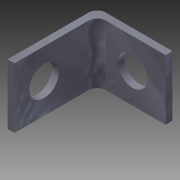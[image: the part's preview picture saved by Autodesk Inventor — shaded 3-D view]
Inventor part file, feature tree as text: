
AUTODESK INVENTOR PART (.ipt)
format: ipt  version: 2016 (Build 200138000, 138)  size: 131,072 bytes
history: native  units: mm
features: sketch x4, projected_geometry x3, extrude x2, hole x2, fillet x1
ambient origin geometry x8: Origin, YZ Plane, XZ Plane, XY Plane, X Axis, Y Axis, Z Axis, Center Point
bodies: Solid1 (feature_tree)
feature tree (12):
  extrude  "BraketBase"  Depth=10.61mm
  extrude  "BraketCut"  Depth=5.305mm
  hole  "ShortHole"  [1 undecoded]
  hole  "LongHole"  [1 undecoded]
  fillet  "Fillet1"  Radius=3.5mm
  sketch  "Sketch1"  dims[d0=8.91mm d1=10.61mm]
  sketch  "Sketch2"  dims[d2=4.455mm d3=5.305mm]
  projected_geometry  "Projected Loop1"
  sketch  "Sketch3"  dims[d4=7.13mm d5=0.0mm d6=0.82mm]
  projected_geometry  "Projected Loop2"
  sketch  "Sketch4"  dims[d7=0.82mm d8=7.13mm d9=0.0mm d10=3.5mm d11=5.0mm d12=3.565mm d13=3.5mm d14=6.0mm d15=4.0mm d16=2.0mm d17=90.0deg d18=8.0mm d19=20.594885mm d20=3.5mm d21=3.5mm d22=3.565mm d23=3.5mm d24=6.0mm d25=4.0mm d26=2.0mm d27=90.0deg d28=8.0mm d29=20.594885mm d30=1.0mm]
  projected_geometry  "Projected Loop3"
note: 2 required parameter values undecoded (feature->parameter linkage not recoverable at this tier; creation-order binding heuristic only, values carry confidence <= 0.55)
